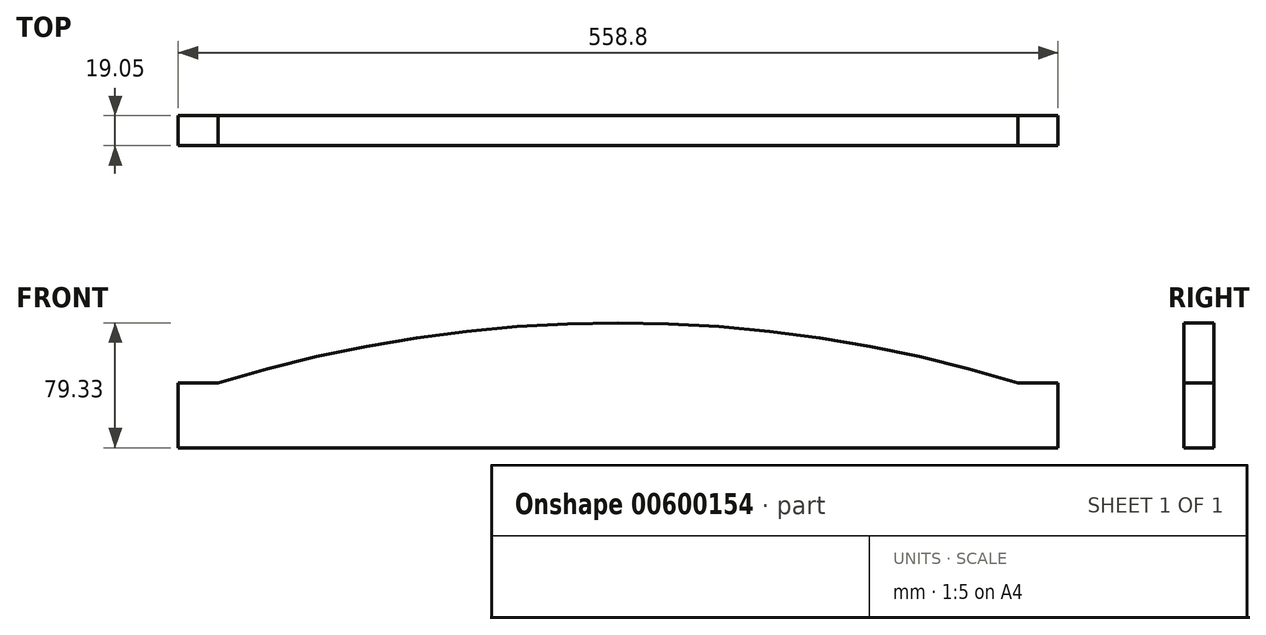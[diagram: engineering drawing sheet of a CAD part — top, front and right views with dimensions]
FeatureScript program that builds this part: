
annotation { "Feature Type Name" : "Feature", "Feature Type Description" : "" }
export const myFeature = defineFeature(function(context is Context, id is Id, definition is map)
    precondition{}
    {
        {
            var Q0;
            Q0=qCreatedBy(makeId("Front.planeOp"),FACE);
            var sketch = newSketch(context, id + "F0", { "sketchPlane" : qUnion([Q0])});
            skLineSegment(sketch, "E0.top", {"start": v(-339.86, -16.23) * mm, "end": v(218.94, -16.23) * mm});
            skLineSegment(sketch, "E0.left", {"start": v(-339.86, 25.05) * mm, "end": v(-339.86, -16.23) * mm});
            skLineSegment(sketch, "E0.right", {"start": v(218.94, 25.05) * mm, "end": v(218.94, -16.23) * mm});
            skLineSegment(sketch, "E1.0", {"start": v(-339.86, 25.05) * mm, "end": v(-314.46, 25.05) * mm});
            skArc(sketch, "E2", {"start": v(193.54, 25.05) * mm, "mid": v(-60.46, 63.1) * mm, "end": v(-314.46, 25.05) * mm});
            skLineSegment(sketch, "E3.trimOffspring", {"start": v(193.54, 25.05) * mm, "end": v(218.94, 25.05) * mm});
            skSolve(sketch);
        }
        {
            var Q0;
            Q0 = qSketchRegion(id + "F0", true);
            extrude(context, id + "F1", {"entities" : qUnion([Q0]), "depth" : 19.05 * mm, "offsetDistance" : 25.4 * mm});
        }
    });
